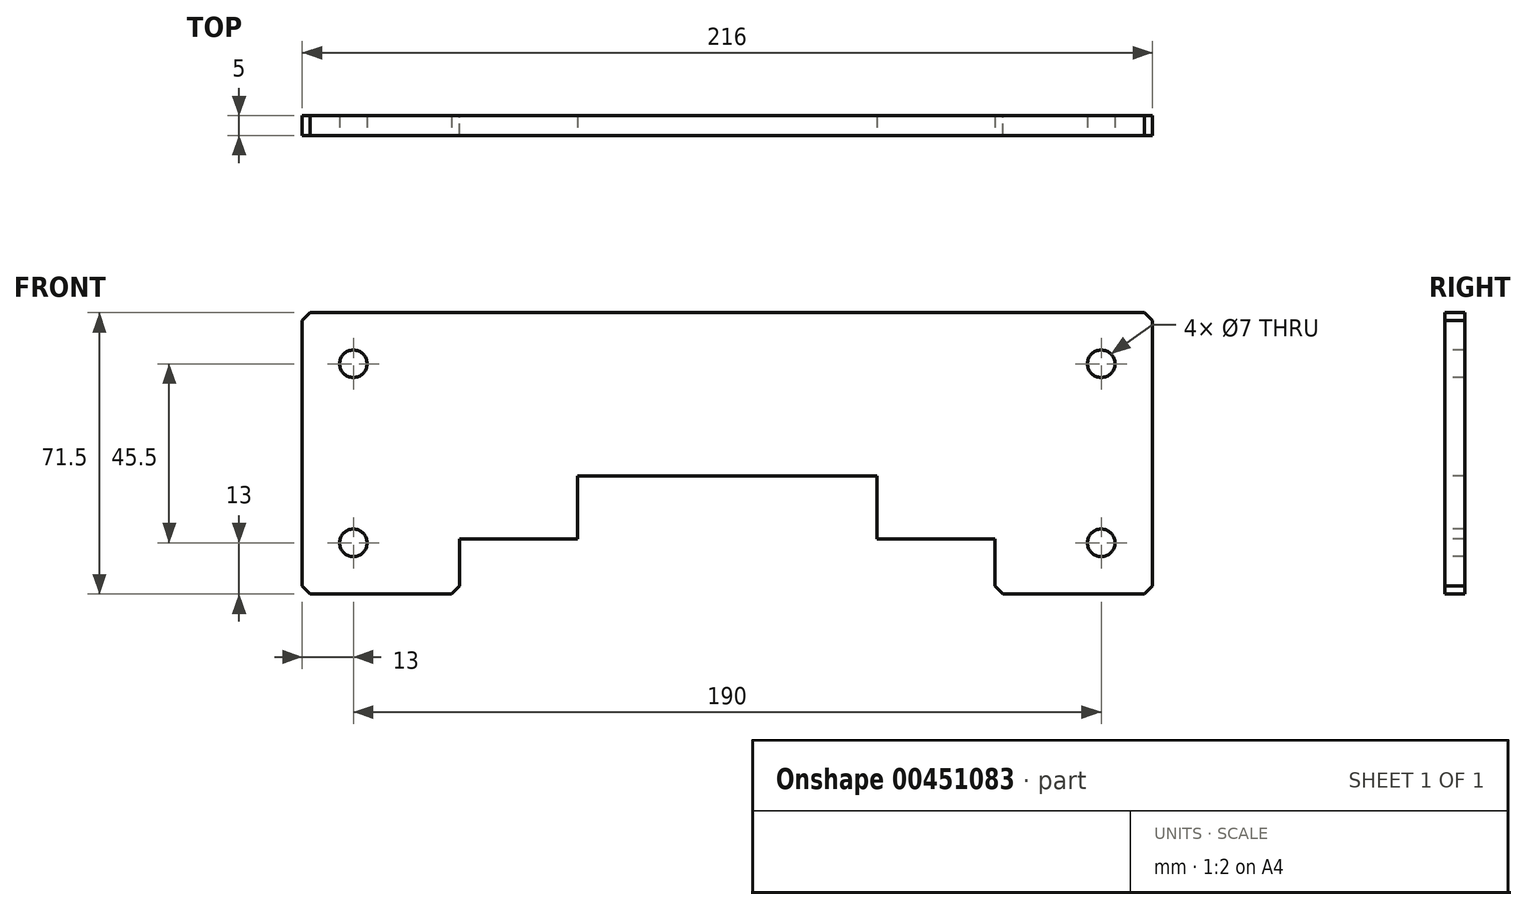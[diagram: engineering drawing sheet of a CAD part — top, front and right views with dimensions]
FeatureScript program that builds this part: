
annotation { "Feature Type Name" : "Feature", "Feature Type Description" : "" }
export const myFeature = defineFeature(function(context is Context, id is Id, definition is map)
    precondition{}
    {
        {
            var Q0;
            Q0=qCreatedBy(makeId("Front.planeOp"),FACE);
            var sketch = newSketch(context, id + "F0", { "sketchPlane" : qUnion([Q0])});
            skLineSegment(sketch, "E0.bottom", {"start": v(0, 0) * mm, "end": v(40, 0) * mm});
            skLineSegment(sketch, "E0.top", {"start": v(0, 71.5) * mm, "end": v(216, 71.5) * mm});
            skLineSegment(sketch, "E0.left", {"start": v(0, 0) * mm, "end": v(0, 71.5) * mm});
            skLineSegment(sketch, "E0.right", {"start": v(216, 0) * mm, "end": v(216, 71.5) * mm});
            skLineSegment(sketch, "E1.0", {"start": v(176, 0) * mm, "end": v(176, 14) * mm});
            skLineSegment(sketch, "E2.0", {"start": v(146, 14) * mm, "end": v(146, 30) * mm});
            skLineSegment(sketch, "E3.0", {"start": v(70, 14) * mm, "end": v(70, 30) * mm});
            skLineSegment(sketch, "E4.0", {"start": v(40, 0) * mm, "end": v(40, 14) * mm});
            skLineSegment(sketch, "E5.0", {"start": v(70, 30) * mm, "end": v(146, 30) * mm});
            skLineSegment(sketch, "E6.0", {"start": v(40, 14) * mm, "end": v(70, 14) * mm});
            skLineSegment(sketch, "E7.trimOffspring", {"start": v(146, 14) * mm, "end": v(176, 14) * mm});
            skLineSegment(sketch, "E8.trimOffspring", {"start": v(176, 0) * mm, "end": v(216, 0) * mm});
            skPoint(sketch, "E9", {"position": v(203, 58.5) * mm});
            skPoint(sketch, "E10", {"position": v(203, 13) * mm});
            skPoint(sketch, "E11.MirrorP", {"position": v(13, 13) * mm});
            skPoint(sketch, "E12.MirrorP", {"position": v(13, 58.5) * mm});
            skSolve(sketch);
        }
        {
            var Q0;
            Q0 = qSketchRegion(id + "F0", true);
            extrude(context, id + "F1", {"entities" : qUnion([Q0]), "oppositeDirection" : true, "depth" : 5 * mm});
        }
        {
            var Q0;
            Q0=sQuery(id+"F0.wireOp",VERTEX,"E9");
            var Q1;
            Q1=sQuery(id+"F0.wireOp",VERTEX,"E10");
            var Q2;
            Q2=sQuery(id+"F0.wireOp",VERTEX,"E11.MirrorP");
            var Q3;
            Q3=sQuery(id+"F0.wireOp",VERTEX,"E12.MirrorP");
            var Q4;
            Q4=makeQuery(id+"F1.opExtrude","SWEPT_BODY",BODY,{"disambiguationData":[OSD([sQuery(id+"F0.wireOp",EDGE,"E0.bottom"),sQuery(id+"F0.wireOp",EDGE,"E0.top"),sQuery(id+"F0.wireOp",EDGE,"E0.left"),sQuery(id+"F0.wireOp",EDGE,"E0.right"),sQuery(id+"F0.wireOp",EDGE,"E1.0"),sQuery(id+"F0.wireOp",EDGE,"E2.0"),sQuery(id+"F0.wireOp",EDGE,"E3.0"),sQuery(id+"F0.wireOp",EDGE,"E4.0"),sQuery(id+"F0.wireOp",EDGE,"E5.0"),sQuery(id+"F0.wireOp",EDGE,"E6.0"),sQuery(id+"F0.wireOp",EDGE,"E7.trimOffspring"),sQuery(id+"F0.wireOp",EDGE,"E8.trimOffspring")])]});
            hole(context, id + "F2", {"style" : HoleStyle.SIMPLE, "endStyle" : HoleEndStyle.THROUGH, "holeDiameter" : 7 * mm, "isTappedThrough" : true, "tappedDepth" : 12 * mm, "tapClearance" : 3, "locations" : qUnion([Q0, Q1, Q2, Q3]), "scope" : qUnion([Q4])});
        }
        {
            var Q0;
            Q0=makeQuery(id+"F1.opExtrude","SWEPT_EDGE",EDGE,{"disambiguationData":[OSD([sQuery(id+"F0.wireOp",EDGE,"E0.top"),sQuery(id+"F0.wireOp",EDGE,"E0.right")])]});
            var Q1;
            Q1=makeQuery(id+"F1.opExtrude","SWEPT_EDGE",EDGE,{"disambiguationData":[OSD([sQuery(id+"F0.wireOp",EDGE,"E0.right"),sQuery(id+"F0.wireOp",EDGE,"E8.trimOffspring")])]});
            var Q2;
            Q2=makeQuery(id+"F1.opExtrude","SWEPT_EDGE",EDGE,{"disambiguationData":[OSD([sQuery(id+"F0.wireOp",EDGE,"E1.0"),sQuery(id+"F0.wireOp",EDGE,"E8.trimOffspring")])]});
            var Q3;
            Q3=makeQuery(id+"F1.opExtrude","SWEPT_EDGE",EDGE,{"disambiguationData":[OSD([sQuery(id+"F0.wireOp",EDGE,"E0.bottom"),sQuery(id+"F0.wireOp",EDGE,"E4.0")])]});
            var Q4;
            Q4=makeQuery(id+"F1.opExtrude","SWEPT_EDGE",EDGE,{"disambiguationData":[OSD([sQuery(id+"F0.wireOp",EDGE,"E0.bottom"),sQuery(id+"F0.wireOp",EDGE,"E0.left")])]});
            var Q5;
            Q5=makeQuery(id+"F1.opExtrude","SWEPT_EDGE",EDGE,{"disambiguationData":[OSD([sQuery(id+"F0.wireOp",EDGE,"E0.top"),sQuery(id+"F0.wireOp",EDGE,"E0.left")])]});
            chamfer(context, id + "F3", {"entities" : qUnion([Q0, Q1, Q2, Q3, Q4, Q5]), "width" : 2 * mm, "tangentPropagation" : true});
        }
    });
